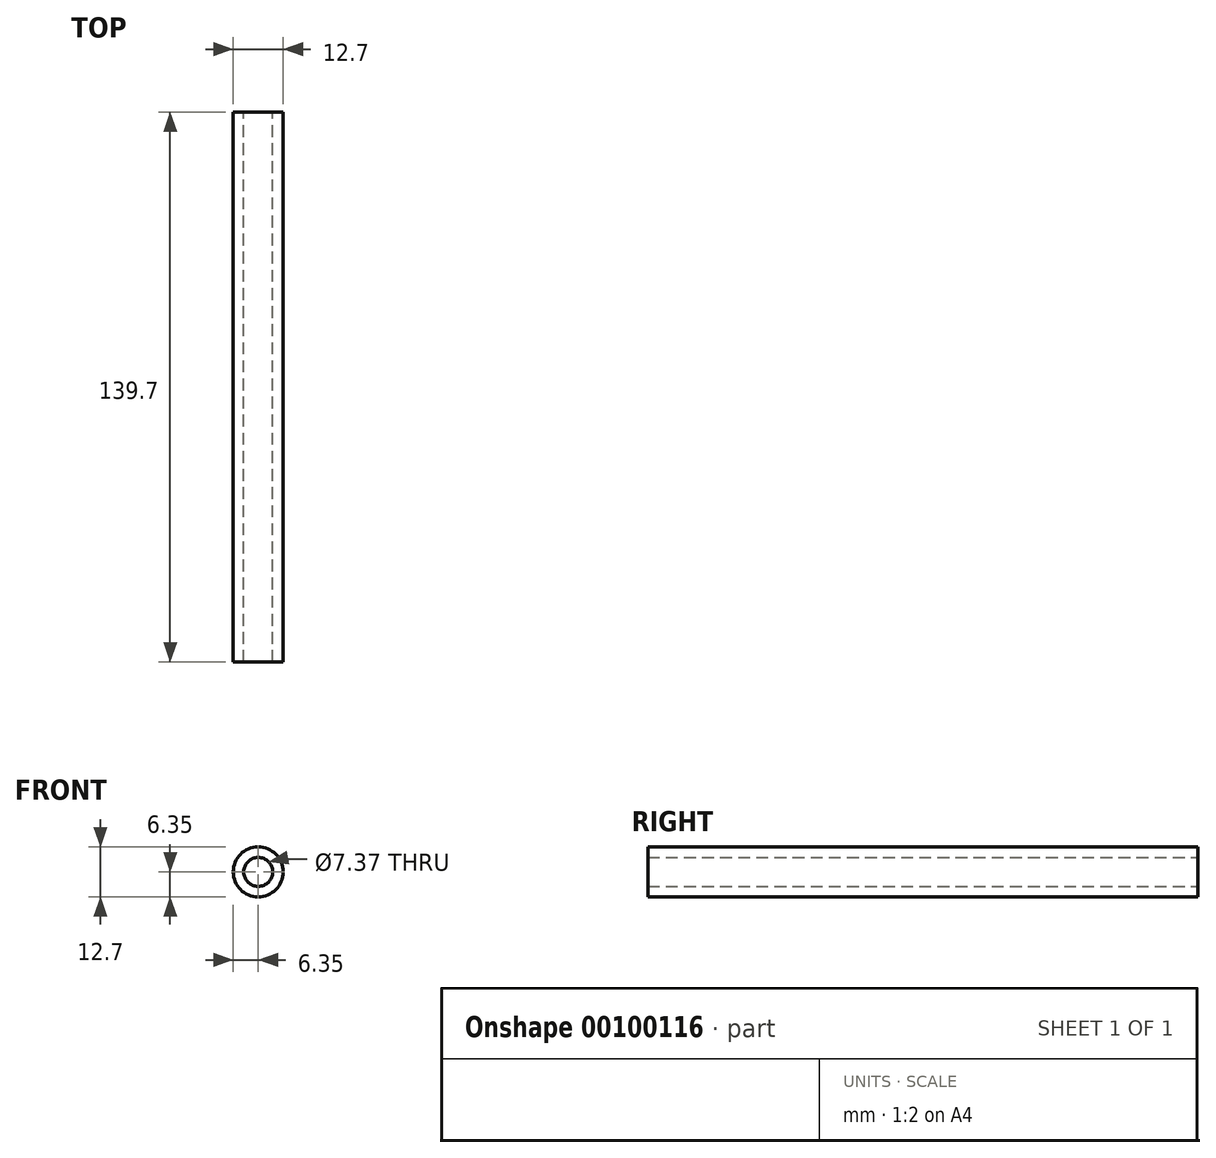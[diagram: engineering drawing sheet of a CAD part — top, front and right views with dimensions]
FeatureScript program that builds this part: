
annotation { "Feature Type Name" : "Feature", "Feature Type Description" : "" }
export const myFeature = defineFeature(function(context is Context, id is Id, definition is map)
    precondition{}
    {
        {
            var Q0;
            Q0=qCreatedBy(makeId("Front.planeOp"),FACE);
            var sketch = newSketch(context, id + "F0", { "sketchPlane" : qUnion([Q0])});
            skCircle(sketch, "E0", {"center": v(0, 0) * mm, "radius": 6.35 * mm});
            skCircle(sketch, "E1", {"center": v(0, 0) * mm, "radius": 3.68 * mm});
            skSolve(sketch);
        }
        {
            var Q0;
            Q0 = qSketchRegion(id + "F0", true);
            extrude(context, id + "F1", {"entities" : qUnion([Q0]), "depth" : 139.7 * mm, "symmetric" : true});
        }
    });
